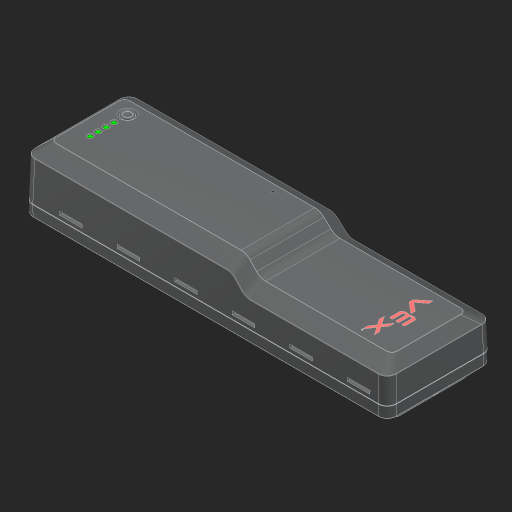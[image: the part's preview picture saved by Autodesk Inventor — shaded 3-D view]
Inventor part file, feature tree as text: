
AUTODESK INVENTOR PART (.ipt)
format: ipt  version: 2023 (Build 270158000, 158)  size: 8,600,576 bytes
history: native  units: in
note: dims shown in document units (in); Inventor stores cm internally (conversion verified against a paired STEP export)
features: other x8, boolean_combine x2, extrude x1, sketch x1
ambient origin geometry x8: Origin, YZ Plane, XZ Plane, XY Plane, X Axis, Y Axis, Z Axis, Center Point
bodies: Solid1 (feature_tree), Solid2 (feature_tree), Solid3 (feature_tree), Solid4 (feature_tree), Solid5 (feature_tree), Solid6 (feature_tree), Solid7 (feature_tree), Solid8 (feature_tree), Solid9 (feature_tree)
feature tree (12):
  extrude  "Extrusion1"  [1 undecoded]
  boolean_combine  "Combine1"
  boolean_combine  "Combine2"
  sketch  "Sketch1"  dims[d14=0.002in d15=0.0in]
  other  "276-4811-001 Rev29_1:1"
  other  "276-4811-002 Rev27_2:1"
  other  "276-4811-011 Rev6_3:1"
  other  "276-4811-013 Rev8_4:1"
  other  "276-4811-013 Rev8_5:1"
  other  "276-4811-013 Rev8_6:1"
  other  "276-4811-013 Rev8_7:1"
  other  "PJ-002A_9:1"
note: 1 required parameter value undecoded (feature->parameter linkage not recoverable at this tier; creation-order binding heuristic only, values carry confidence <= 0.55)
